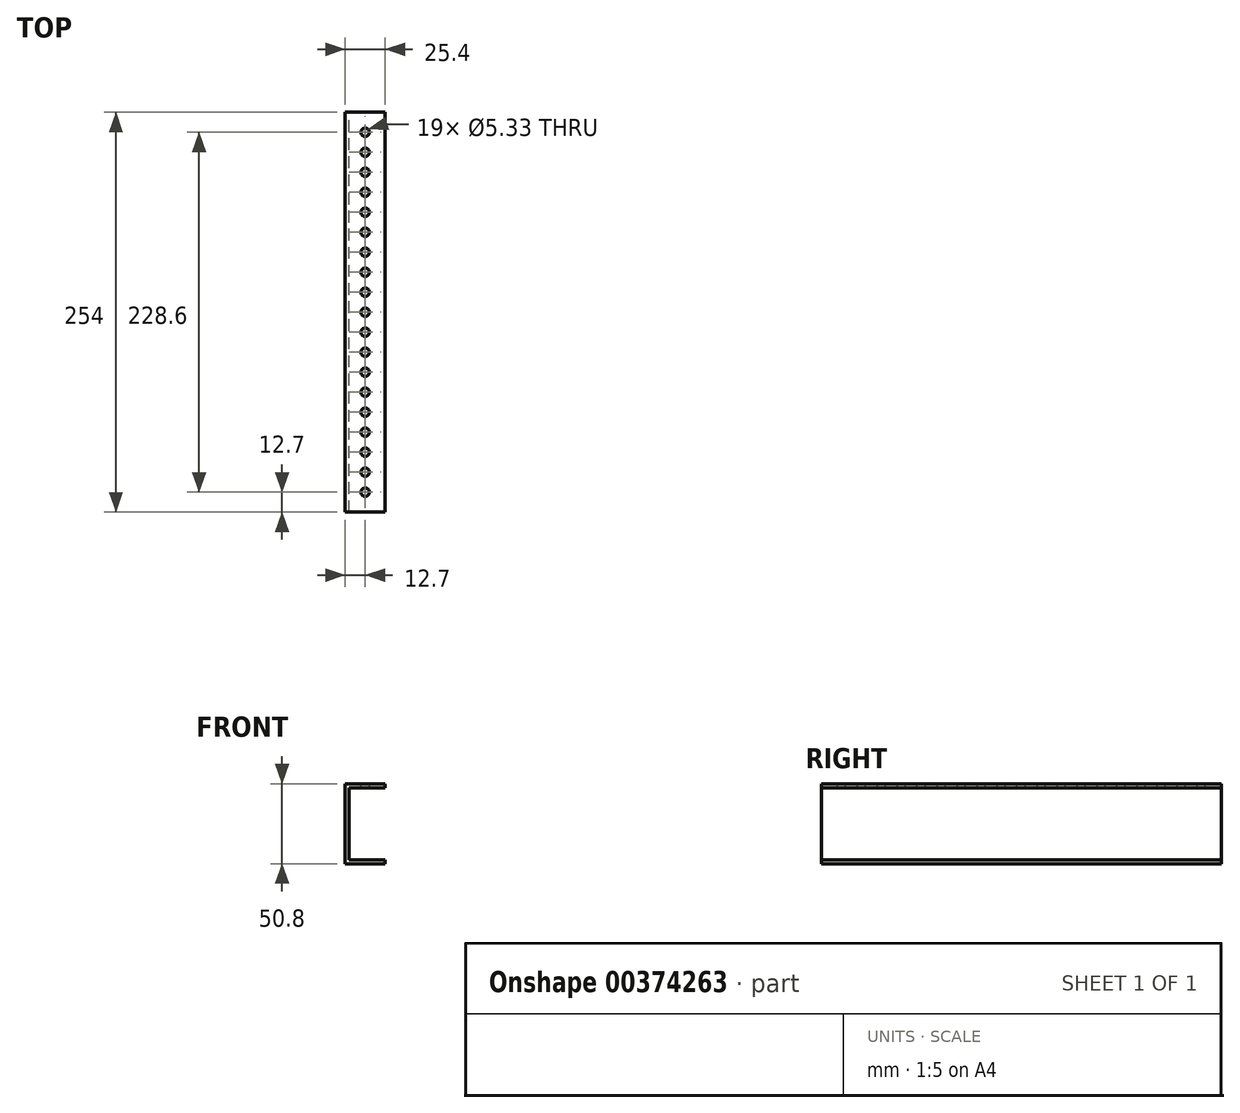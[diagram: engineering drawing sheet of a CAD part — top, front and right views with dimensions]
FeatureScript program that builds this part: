
annotation { "Feature Type Name" : "Feature", "Feature Type Description" : "" }
export const myFeature = defineFeature(function(context is Context, id is Id, definition is map)
    precondition{}
    {
        {
            var Q0;
            Q0=qCreatedBy(makeId("Front.planeOp"),FACE);
            var sketch = newSketch(context, id + "F0", { "sketchPlane" : qUnion([Q0])});
            skLineSegment(sketch, "E0", {"start": v(25.4, 25.4) * mm, "end": v(0, 25.4) * mm});
            skLineSegment(sketch, "E1", {"start": v(0, 25.4) * mm, "end": v(0, -25.4) * mm});
            skLineSegment(sketch, "E2", {"start": v(0, -25.4) * mm, "end": v(25.4, -25.4) * mm});
            skLineSegment(sketch, "E3.0", {"start": v(2.54, -22.86) * mm, "end": v(25.4, -22.86) * mm});
            skLineSegment(sketch, "E3.1", {"start": v(2.54, 22.86) * mm, "end": v(2.54, -22.86) * mm});
            skLineSegment(sketch, "E3.2", {"start": v(25.4, 22.86) * mm, "end": v(2.54, 22.86) * mm});
            skLineSegment(sketch, "E4", {"start": v(25.4, 25.4) * mm, "end": v(25.4, 22.86) * mm});
            skLineSegment(sketch, "E5", {"start": v(25.4, -22.86) * mm, "end": v(25.4, -25.4) * mm});
            skLineSegment(sketch, "E6", {"start": v(0, 62.94) * mm, "end": v(0, -58.06) * mm, "construction": true});
            skLineSegment(sketch, "E7", {"start": v(0, 0) * mm, "end": v(0, -25.4) * mm, "construction": true});
            skSolve(sketch);
        }
        {
            var Q0;
            Q0=makeQuery(id+"F0.imprint","IMPRINT",FACE,{"disambiguationData":[TD([[makeQuery(id+"F0.imprint","IMPRINT",EDGE,{"derivedFrom":sQuery(id+"F0.wireOp",EDGE,"E0")}),1.0]])]});
            extrude(context, id + "F1", {"entities" : qUnion([Q0]), "endBound" : BoundingType.SYMMETRIC, "depth" : 254 * mm});
        }
        {
            var Q0;
            Q0=makeQuery(id+"F1.opExtrude","SWEPT_FACE",FACE,{"disambiguationData":[OSD([sQuery(id+"F0.wireOp",EDGE,"E0")])]});
            var sketch = newSketch(context, id + "F2", { "sketchPlane" : qUnion([Q0])});
            skLineSegment(sketch, "E8", {"start": v(12.7, 127) * mm, "end": v(12.7, -127) * mm, "construction": true});
            skCircle(sketch, "E9", {"center": v(12.7, 114.3) * mm, "radius": 2.67 * mm});
            skCircle(sketch, "E10.1.0.0", {"center": v(12.7, 101.6) * mm, "radius": 2.67 * mm});
            skCircle(sketch, "E10.2.0.0", {"center": v(12.7, 88.9) * mm, "radius": 2.67 * mm});
            skCircle(sketch, "E10.3.0.0", {"center": v(12.7, 76.2) * mm, "radius": 2.67 * mm});
            skCircle(sketch, "E10.4.0.0", {"center": v(12.7, 63.5) * mm, "radius": 2.67 * mm});
            skCircle(sketch, "E10.5.0.0", {"center": v(12.7, 50.8) * mm, "radius": 2.67 * mm});
            skCircle(sketch, "E10.6.0.0", {"center": v(12.7, 38.1) * mm, "radius": 2.67 * mm});
            skCircle(sketch, "E10.7.0.0", {"center": v(12.7, 25.4) * mm, "radius": 2.67 * mm});
            skCircle(sketch, "E10.8.0.0", {"center": v(12.7, 12.7) * mm, "radius": 2.67 * mm});
            skCircle(sketch, "E10.9.0.0", {"center": v(12.7, 0) * mm, "radius": 2.67 * mm});
            skCircle(sketch, "E10.10.0.0", {"center": v(12.7, -12.7) * mm, "radius": 2.67 * mm});
            skCircle(sketch, "E10.11.0.0", {"center": v(12.7, -25.4) * mm, "radius": 2.67 * mm});
            skCircle(sketch, "E10.12.0.0", {"center": v(12.7, -38.1) * mm, "radius": 2.67 * mm});
            skCircle(sketch, "E10.13.0.0", {"center": v(12.7, -50.8) * mm, "radius": 2.67 * mm});
            skCircle(sketch, "E10.14.0.0", {"center": v(12.7, -63.5) * mm, "radius": 2.67 * mm});
            skCircle(sketch, "E10.15.0.0", {"center": v(12.7, -76.2) * mm, "radius": 2.67 * mm});
            skCircle(sketch, "E10.16.0.0", {"center": v(12.7, -88.9) * mm, "radius": 2.67 * mm});
            skCircle(sketch, "E10.17.0.0", {"center": v(12.7, -101.6) * mm, "radius": 2.67 * mm});
            skCircle(sketch, "E10.18.0.0", {"center": v(12.7, -114.3) * mm, "radius": 2.67 * mm});
            skLineSegment(sketch, "E10.direction1", {"start": v(12.7, 114.3) * mm, "end": v(12.7, 101.6) * mm, "construction": true});
            skSolve(sketch);
        }
        {
            var Q0;
            Q0=makeQuery(id+"F2.imprint","IMPRINT",FACE,{"disambiguationData":[TD([[makeQuery(id+"F2.imprint","IMPRINT",EDGE,{"derivedFrom":sQuery(id+"F2.wireOp",EDGE,"E10.13.0.0")}),1.0]])]});
            var Q1;
            Q1=makeQuery(id+"F2.imprint","IMPRINT",FACE,{"disambiguationData":[TD([[makeQuery(id+"F2.imprint","IMPRINT",EDGE,{"derivedFrom":sQuery(id+"F2.wireOp",EDGE,"E10.14.0.0")}),1.0]])]});
            var Q2;
            Q2=makeQuery(id+"F2.imprint","IMPRINT",FACE,{"disambiguationData":[TD([[makeQuery(id+"F2.imprint","IMPRINT",EDGE,{"derivedFrom":sQuery(id+"F2.wireOp",EDGE,"E10.18.0.0")}),1.0]])]});
            var Q3;
            Q3=makeQuery(id+"F2.imprint","IMPRINT",FACE,{"disambiguationData":[TD([[makeQuery(id+"F2.imprint","IMPRINT",EDGE,{"derivedFrom":sQuery(id+"F2.wireOp",EDGE,"E10.1.0.0")}),1.0]])]});
            var Q4;
            Q4=makeQuery(id+"F2.imprint","IMPRINT",FACE,{"disambiguationData":[TD([[makeQuery(id+"F2.imprint","IMPRINT",EDGE,{"derivedFrom":sQuery(id+"F2.wireOp",EDGE,"E10.15.0.0")}),1.0]])]});
            var Q5;
            Q5=makeQuery(id+"F2.imprint","IMPRINT",FACE,{"disambiguationData":[TD([[makeQuery(id+"F2.imprint","IMPRINT",EDGE,{"derivedFrom":sQuery(id+"F2.wireOp",EDGE,"E10.3.0.0")}),1.0]])]});
            var Q6;
            Q6=makeQuery(id+"F2.imprint","IMPRINT",FACE,{"disambiguationData":[TD([[makeQuery(id+"F2.imprint","IMPRINT",EDGE,{"derivedFrom":sQuery(id+"F2.wireOp",EDGE,"E10.2.0.0")}),1.0]])]});
            var Q7;
            Q7=makeQuery(id+"F2.imprint","IMPRINT",FACE,{"disambiguationData":[TD([[makeQuery(id+"F2.imprint","IMPRINT",EDGE,{"derivedFrom":sQuery(id+"F2.wireOp",EDGE,"E10.5.0.0")}),1.0]])]});
            var Q8;
            Q8=makeQuery(id+"F2.imprint","IMPRINT",FACE,{"disambiguationData":[TD([[makeQuery(id+"F2.imprint","IMPRINT",EDGE,{"derivedFrom":sQuery(id+"F2.wireOp",EDGE,"E10.17.0.0")}),1.0]])]});
            var Q9;
            Q9=makeQuery(id+"F2.imprint","IMPRINT",FACE,{"disambiguationData":[TD([[makeQuery(id+"F2.imprint","IMPRINT",EDGE,{"derivedFrom":sQuery(id+"F2.wireOp",EDGE,"E10.11.0.0")}),1.0]])]});
            var Q10;
            Q10=makeQuery(id+"F2.imprint","IMPRINT",FACE,{"disambiguationData":[TD([[makeQuery(id+"F2.imprint","IMPRINT",EDGE,{"derivedFrom":sQuery(id+"F2.wireOp",EDGE,"E10.12.0.0")}),1.0]])]});
            var Q11;
            Q11=makeQuery(id+"F2.imprint","IMPRINT",FACE,{"disambiguationData":[TD([[makeQuery(id+"F2.imprint","IMPRINT",EDGE,{"derivedFrom":sQuery(id+"F2.wireOp",EDGE,"E10.8.0.0")}),1.0]])]});
            var Q12;
            Q12=makeQuery(id+"F2.imprint","IMPRINT",FACE,{"disambiguationData":[TD([[makeQuery(id+"F2.imprint","IMPRINT",EDGE,{"derivedFrom":sQuery(id+"F2.wireOp",EDGE,"E10.16.0.0")}),1.0]])]});
            var Q13;
            Q13=makeQuery(id+"F2.imprint","IMPRINT",FACE,{"disambiguationData":[TD([[makeQuery(id+"F2.imprint","IMPRINT",EDGE,{"derivedFrom":sQuery(id+"F2.wireOp",EDGE,"E10.10.0.0")}),1.0]])]});
            var Q14;
            Q14=makeQuery(id+"F2.imprint","IMPRINT",FACE,{"disambiguationData":[TD([[makeQuery(id+"F2.imprint","IMPRINT",EDGE,{"derivedFrom":sQuery(id+"F2.wireOp",EDGE,"E10.7.0.0")}),1.0]])]});
            var Q15;
            Q15=makeQuery(id+"F2.imprint","IMPRINT",FACE,{"disambiguationData":[TD([[makeQuery(id+"F2.imprint","IMPRINT",EDGE,{"derivedFrom":sQuery(id+"F2.wireOp",EDGE,"E10.6.0.0")}),1.0]])]});
            var Q16;
            Q16=makeQuery(id+"F2.imprint","IMPRINT",FACE,{"disambiguationData":[TD([[makeQuery(id+"F2.imprint","IMPRINT",EDGE,{"derivedFrom":sQuery(id+"F2.wireOp",EDGE,"E10.9.0.0")}),1.0]])]});
            var Q17;
            Q17=makeQuery(id+"F2.imprint","IMPRINT",FACE,{"disambiguationData":[TD([[makeQuery(id+"F2.imprint","IMPRINT",EDGE,{"derivedFrom":sQuery(id+"F2.wireOp",EDGE,"E10.4.0.0")}),1.0]])]});
            var Q18;
            Q18=makeQuery(id+"F2.imprint","IMPRINT",FACE,{"disambiguationData":[TD([[makeQuery(id+"F2.imprint","IMPRINT",EDGE,{"derivedFrom":sQuery(id+"F2.wireOp",EDGE,"E9")}),1.0]])]});
            var Q19;
            Q19=sQuery(id+"F2.wireOp",EDGE,"E10.18.0.0");
            var Q20;
            Q20=sQuery(id+"F2.wireOp",EDGE,"E10.17.0.0");
            var Q21;
            Q21=sQuery(id+"F2.wireOp",EDGE,"E10.16.0.0");
            var Q22;
            Q22=sQuery(id+"F2.wireOp",EDGE,"E10.15.0.0");
            var Q23;
            Q23=sQuery(id+"F2.wireOp",EDGE,"E10.14.0.0");
            var Q24;
            Q24=sQuery(id+"F2.wireOp",EDGE,"E10.13.0.0");
            var Q25;
            Q25=sQuery(id+"F2.wireOp",EDGE,"E10.12.0.0");
            var Q26;
            Q26=sQuery(id+"F2.wireOp",EDGE,"E10.11.0.0");
            var Q27;
            Q27=sQuery(id+"F2.wireOp",EDGE,"E10.10.0.0");
            var Q28;
            Q28=sQuery(id+"F2.wireOp",EDGE,"E10.9.0.0");
            var Q29;
            Q29=sQuery(id+"F2.wireOp",EDGE,"E10.8.0.0");
            var Q30;
            Q30=sQuery(id+"F2.wireOp",EDGE,"E10.7.0.0");
            var Q31;
            Q31=sQuery(id+"F2.wireOp",EDGE,"E10.6.0.0");
            var Q32;
            Q32=sQuery(id+"F2.wireOp",EDGE,"E10.5.0.0");
            var Q33;
            Q33=sQuery(id+"F2.wireOp",EDGE,"E10.4.0.0");
            var Q34;
            Q34=sQuery(id+"F2.wireOp",EDGE,"E10.3.0.0");
            var Q35;
            Q35=sQuery(id+"F2.wireOp",EDGE,"E10.2.0.0");
            var Q36;
            Q36=sQuery(id+"F2.wireOp",EDGE,"E10.1.0.0");
            var Q37;
            Q37=sQuery(id+"F2.wireOp",EDGE,"E9");
            extrude(context, id + "F3", {"entities" : qUnion([Q0, Q1, Q2, Q3, Q4, Q5, Q6, Q7, Q8, Q9, Q10, Q11, Q12, Q13, Q14, Q15, Q16, Q17, Q18]), "operationType" : NewBodyOperationType.REMOVE, "surfaceEntities" : qUnion([Q19, Q20, Q21, Q22, Q23, Q24, Q25, Q26, Q27, Q28, Q29, Q30, Q31, Q32, Q33, Q34, Q35, Q36, Q37]), "oppositeDirection" : true, "depth" : 2.54 * mm});
        }
    });
